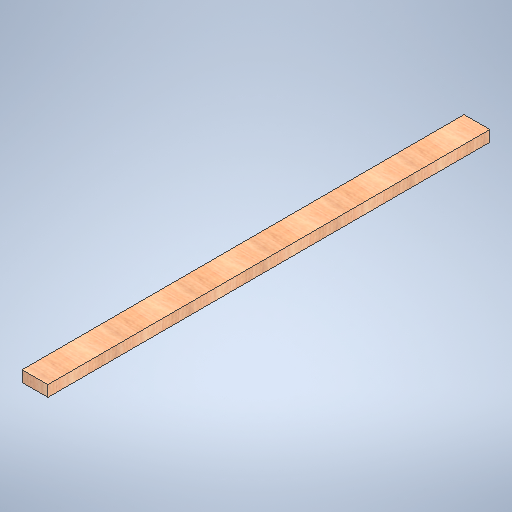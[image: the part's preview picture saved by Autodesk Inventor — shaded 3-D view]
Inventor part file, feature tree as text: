
AUTODESK INVENTOR PART (.ipt)
format: ipt  version: 2025 (Build 290162010, 162A)  size: 290,816 bytes
history: native  units: in
note: dims shown in document units (in); Inventor stores cm internally (conversion verified against a paired STEP export)
features: extrude x1, sketch x1
ambient origin geometry x8: Origin, YZ Plane, XZ Plane, XY Plane, X Axis, Y Axis, Z Axis, Center Point
bodies: Solid1 (feature_tree)
feature tree (2):
  extrude  "Extrusion1"  Depth=1.5in TaperAngle=0.0deg
  sketch  "Sketch1"  dims[d1=3.5in d2=1.5in d3=0.0in d4=60.0in]
